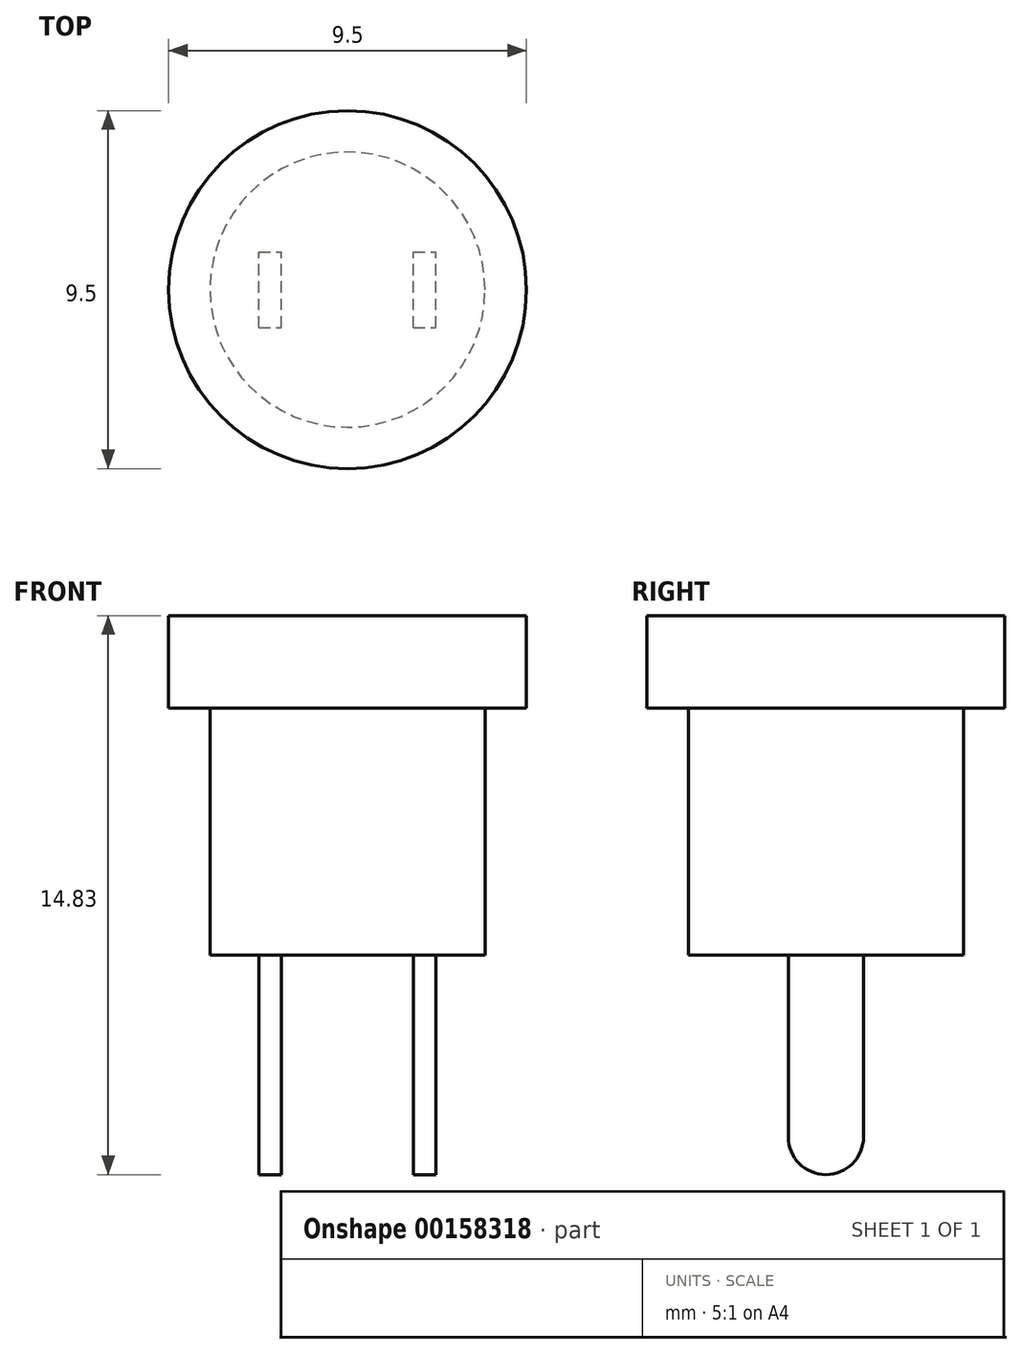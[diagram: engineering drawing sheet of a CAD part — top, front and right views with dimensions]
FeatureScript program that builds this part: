
annotation { "Feature Type Name" : "Feature", "Feature Type Description" : "" }
export const myFeature = defineFeature(function(context is Context, id is Id, definition is map)
    precondition{}
    {
        {
            var Q0;
            Q0=qCreatedBy(makeId("Top.planeOp"),FACE);
            var sketch = newSketch(context, id + "F0", { "sketchPlane" : qUnion([Q0])});
            skCircle(sketch, "E0", {"center": v(0, 0) * mm, "radius": 4.75 * mm});
            skSolve(sketch);
        }
        {
            var Q0;
            Q0=makeQuery(id+"F0.imprint","IMPRINT",FACE,{"disambiguationData":[TD([[makeQuery(id+"F0.imprint","IMPRINT",EDGE,{"derivedFrom":sQuery(id+"F0.wireOp",EDGE,"E0")}),1.0]])]});
            extrude(context, id + "F1", {"entities" : qUnion([Q0]), "oppositeDirection" : true, "depth" : 2.45 * mm});
        }
        {
            var Q0;
            Q0=makeQuery(id+"F1.opExtrude","CAP_FACE",FACE,{"disambiguationData":[OSD([sQuery(id+"F0.wireOp",EDGE,"E0")])],"isStart":false});
            var sketch = newSketch(context, id + "F2", { "sketchPlane" : qUnion([Q0])});
            skCircle(sketch, "E1", {"center": v(0, 0) * mm, "radius": 3.65 * mm});
            skSolve(sketch);
        }
        {
            var Q0;
            Q0=makeQuery(id+"F2.imprint","IMPRINT",FACE,{"disambiguationData":[TD([[makeQuery(id+"F2.imprint","IMPRINT",EDGE,{"derivedFrom":sQuery(id+"F2.wireOp",EDGE,"E1")}),1.0]])]});
            extrude(context, id + "F3", {"entities" : qUnion([Q0]), "operationType" : NewBodyOperationType.ADD, "depth" : 6.55 * mm});
        }
        {
            var Q0;
            Q0=makeQuery(id+"F3.opExtrude","CAP_FACE",FACE,{"disambiguationData":[OSD([sQuery(id+"F2.wireOp",EDGE,"E1")])],"isStart":false});
            var sketch = newSketch(context, id + "F4", { "sketchPlane" : qUnion([Q0])});
            skCircle(sketch, "E2", {"center": v(0, 0) * mm, "radius": 1.75 * mm, "construction": true});
            skLineSegment(sketch, "E3", {"start": v(-1.75, 0) * mm, "end": v(1.75, 0) * mm, "construction": true});
            skLineSegment(sketch, "E4", {"start": v(0, 1.75) * mm, "end": v(0, -1.75) * mm, "construction": true});
            skLineSegment(sketch, "E5.bottom", {"start": v(-2.35, 1) * mm, "end": v(-1.75, 1) * mm});
            skLineSegment(sketch, "E5.top", {"start": v(-2.35, -1) * mm, "end": v(-1.75, -1) * mm});
            skLineSegment(sketch, "E5.left", {"start": v(-2.35, 1) * mm, "end": v(-2.35, -1) * mm});
            skLineSegment(sketch, "E5.right", {"start": v(-1.75, 1) * mm, "end": v(-1.75, -1) * mm});
            skLineSegment(sketch, "E6.bottom", {"start": v(1.75, 1) * mm, "end": v(2.35, 1) * mm});
            skLineSegment(sketch, "E6.top", {"start": v(1.75, -1) * mm, "end": v(2.35, -1) * mm});
            skLineSegment(sketch, "E6.left", {"start": v(1.75, 1) * mm, "end": v(1.75, -1) * mm});
            skLineSegment(sketch, "E6.right", {"start": v(2.35, 1) * mm, "end": v(2.35, -1) * mm});
            skSolve(sketch);
        }
        {
            var Q0;
            Q0=makeQuery(id+"F4.imprint","IMPRINT",FACE,{"disambiguationData":[TD([[makeQuery(id+"F4.imprint","IMPRINT",EDGE,{"derivedFrom":sQuery(id+"F4.wireOp",EDGE,"E5.bottom")}),-1.0]])]});
            var Q1;
            Q1=makeQuery(id+"F4.imprint","IMPRINT",FACE,{"disambiguationData":[TD([[makeQuery(id+"F4.imprint","IMPRINT",EDGE,{"derivedFrom":sQuery(id+"F4.wireOp",EDGE,"E6.bottom")}),-1.0]])]});
            extrude(context, id + "F5", {"entities" : qUnion([Q0, Q1]), "operationType" : NewBodyOperationType.ADD, "depth" : 5.83 * mm});
        }
        {
            var Q0;
            Q0=makeQuery(id+"F5.opExtrude","CAP_EDGE",EDGE,{"disambiguationData":[OSD([sQuery(id+"F4.wireOp",EDGE,"E5.bottom")])],"isStart":false});
            var Q1;
            Q1=makeQuery(id+"F5.opExtrude","CAP_EDGE",EDGE,{"disambiguationData":[OSD([sQuery(id+"F4.wireOp",EDGE,"E6.bottom")])],"isStart":false});
            var Q2;
            Q2=makeQuery(id+"F5.opExtrude","CAP_EDGE",EDGE,{"disambiguationData":[OSD([sQuery(id+"F4.wireOp",EDGE,"E6.top")])],"isStart":false});
            var Q3;
            Q3=makeQuery(id+"F5.opExtrude","CAP_EDGE",EDGE,{"disambiguationData":[OSD([sQuery(id+"F4.wireOp",EDGE,"E5.top")])],"isStart":false});
            fillet(context, id + "F6", {"entities" : qUnion([Q0, Q1, Q2, Q3]), "radius" : 1 * mm, "tangentPropagation" : true, "allowEdgeOverflow" : false});
        }
    });
